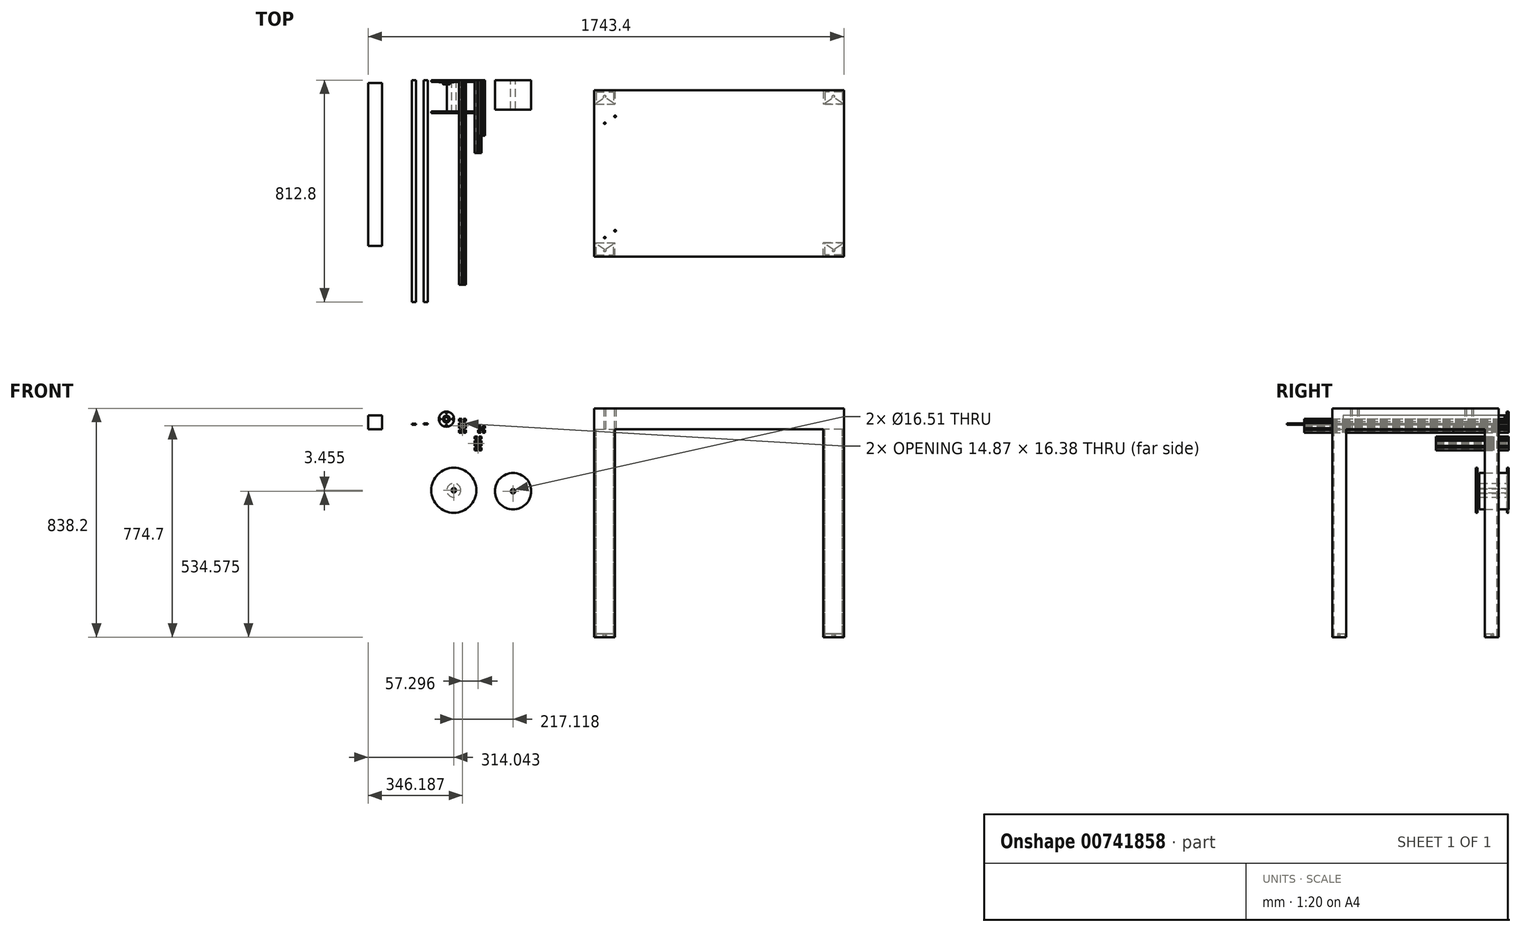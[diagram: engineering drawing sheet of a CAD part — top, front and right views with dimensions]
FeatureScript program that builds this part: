
annotation { "Feature Type Name" : "Feature", "Feature Type Description" : "" }
export const myFeature = defineFeature(function(context is Context, id is Id, definition is map)
    precondition{}
    {
        {
            var Q0;
            Q0=qCreatedBy(makeId("Front.planeOp"),FACE);
            var sketch = newSketch(context, id + "F0", { "sketchPlane" : qUnion([Q0])});
            skCircle(sketch, "E0", {"center": v(0, 0) * mm, "radius": 2.6 * mm});
            skLineSegment(sketch, "E1.bottom", {"start": v(-4.5, 4.5) * mm, "end": v(4.5, 4.5) * mm});
            skLineSegment(sketch, "E1.top", {"start": v(-4.5, -4.5) * mm, "end": v(4.5, -4.5) * mm});
            skLineSegment(sketch, "E1.left", {"start": v(-4.5, 4.5) * mm, "end": v(-4.5, -4.5) * mm});
            skLineSegment(sketch, "E1.right", {"start": v(4.5, 4.5) * mm, "end": v(4.5, -4.5) * mm});
            skLineSegment(sketch, "E2.bottom", {"start": v(-12.7, 12.7) * mm, "end": v(12.7, 12.7) * mm});
            skLineSegment(sketch, "E2.top", {"start": v(-12.7, -12.7) * mm, "end": v(12.7, -12.7) * mm});
            skLineSegment(sketch, "E2.left", {"start": v(-12.7, 12.7) * mm, "end": v(-12.7, -12.7) * mm});
            skLineSegment(sketch, "E2.right", {"start": v(12.7, 12.7) * mm, "end": v(12.7, -12.7) * mm});
            skLineSegment(sketch, "E3.bottom", {"start": v(-3.24, 12.7) * mm, "end": v(3.24, 12.7) * mm});
            skLineSegment(sketch, "E3.top", {"start": v(-3.24, 4.5) * mm, "end": v(3.24, 4.5) * mm});
            skLineSegment(sketch, "E3.left", {"start": v(-3.24, 12.7) * mm, "end": v(-3.24, 10.5) * mm});
            skLineSegment(sketch, "E3.right", {"start": v(3.24, 12.7) * mm, "end": v(3.24, 10.5) * mm});
            skLineSegment(sketch, "E4.bottom", {"start": v(-7.43, 10.5) * mm, "end": v(-3.24, 10.5) * mm});
            skLineSegment(sketch, "E5", {"start": v(-7.43, 10.5) * mm, "end": v(-3.24, 4.5) * mm});
            skLineSegment(sketch, "E6", {"start": v(3.24, 4.5) * mm, "end": v(7.43, 10.5) * mm});
            skLineSegment(sketch, "E7.trimOffspring", {"start": v(3.24, 10.5) * mm, "end": v(7.43, 10.5) * mm});
            skLineSegment(sketch, "E8.bottom", {"start": v(-12.7, 3.24) * mm, "end": v(-10.5, 3.24) * mm});
            skLineSegment(sketch, "E8.top", {"start": v(-12.7, -3.24) * mm, "end": v(-10.5, -3.24) * mm});
            skLineSegment(sketch, "E8.left", {"start": v(-12.7, 3.24) * mm, "end": v(-12.7, -3.24) * mm});
            skLineSegment(sketch, "E8.right", {"start": v(-4.5, 3.24) * mm, "end": v(-4.5, -3.24) * mm});
            skLineSegment(sketch, "E9.left", {"start": v(-10.5, 7.43) * mm, "end": v(-10.5, 3.24) * mm});
            skLineSegment(sketch, "E10", {"start": v(-10.5, 7.43) * mm, "end": v(-4.5, 3.24) * mm});
            skLineSegment(sketch, "E11.trimOffspring", {"start": v(-10.5, -3.24) * mm, "end": v(-10.5, -7.43) * mm});
            skLineSegment(sketch, "E12.MirrorCS", {"start": v(-3.24, -12.7) * mm, "end": v(-3.24, -10.5) * mm});
            skLineSegment(sketch, "E13.MirrorCS", {"start": v(-7.43, -10.5) * mm, "end": v(-3.24, -10.5) * mm});
            skLineSegment(sketch, "E14.MirrorCS", {"start": v(-7.43, -10.5) * mm, "end": v(-3.24, -4.5) * mm});
            skLineSegment(sketch, "E15.MirrorCS", {"start": v(3.24, -4.5) * mm, "end": v(7.43, -10.5) * mm});
            skLineSegment(sketch, "E16.MirrorCS", {"start": v(3.24, -10.5) * mm, "end": v(7.43, -10.5) * mm});
            skLineSegment(sketch, "E17.MirrorCS", {"start": v(3.24, -12.7) * mm, "end": v(3.24, -10.5) * mm});
            skLineSegment(sketch, "E18.MirrorCS", {"start": v(10.5, 7.43) * mm, "end": v(4.5, 3.24) * mm});
            skLineSegment(sketch, "E19.MirrorCS", {"start": v(10.5, -3.24) * mm, "end": v(10.5, -7.43) * mm});
            skLineSegment(sketch, "E20.MirrorCS", {"start": v(12.7, -3.24) * mm, "end": v(10.5, -3.24) * mm});
            skLineSegment(sketch, "E21.MirrorCS", {"start": v(12.7, 3.24) * mm, "end": v(10.5, 3.24) * mm});
            skLineSegment(sketch, "E22.MirrorCS", {"start": v(10.5, 7.43) * mm, "end": v(10.5, 3.24) * mm});
            skLineSegment(sketch, "E23", {"start": v(-10.5, -7.43) * mm, "end": v(-4.5, -3.24) * mm});
            skLineSegment(sketch, "E24", {"start": v(4.5, -3.24) * mm, "end": v(10.5, -7.43) * mm});
            skCircle(sketch, "E25", {"center": v(0, 25.4) * mm, "radius": 2.6 * mm});
            skLineSegment(sketch, "E26.bottom", {"start": v(-4.5, 29.9) * mm, "end": v(4.5, 29.9) * mm});
            skLineSegment(sketch, "E26.top", {"start": v(-4.5, 20.9) * mm, "end": v(4.5, 20.9) * mm});
            skLineSegment(sketch, "E26.left", {"start": v(-4.5, 29.9) * mm, "end": v(-4.5, 20.9) * mm});
            skLineSegment(sketch, "E26.right", {"start": v(4.5, 29.9) * mm, "end": v(4.5, 20.9) * mm});
            skLineSegment(sketch, "E27.bottom", {"start": v(-12.7, 38.1) * mm, "end": v(12.7, 38.1) * mm});
            skLineSegment(sketch, "E27.left", {"start": v(-12.7, 38.1) * mm, "end": v(-12.7, 12.7) * mm});
            skLineSegment(sketch, "E27.right", {"start": v(12.7, 38.1) * mm, "end": v(12.7, 12.7) * mm});
            skLineSegment(sketch, "E28.bottom", {"start": v(-3.24, 38.1) * mm, "end": v(3.24, 38.1) * mm});
            skLineSegment(sketch, "E28.top", {"start": v(-3.24, 29.9) * mm, "end": v(3.24, 29.9) * mm});
            skLineSegment(sketch, "E28.left", {"start": v(-3.24, 38.1) * mm, "end": v(-3.24, 35.9) * mm});
            skLineSegment(sketch, "E28.right", {"start": v(3.24, 38.1) * mm, "end": v(3.24, 35.9) * mm});
            skLineSegment(sketch, "E29.bottom", {"start": v(-7.44, 35.9) * mm, "end": v(-3.24, 35.9) * mm});
            skLineSegment(sketch, "E30", {"start": v(-7.44, 35.9) * mm, "end": v(-3.24, 29.9) * mm});
            skLineSegment(sketch, "E31", {"start": v(3.24, 29.9) * mm, "end": v(7.42, 35.9) * mm});
            skLineSegment(sketch, "E32.trimOffspring", {"start": v(3.24, 35.9) * mm, "end": v(7.42, 35.9) * mm});
            skLineSegment(sketch, "E33.bottom", {"start": v(-12.7, 28.64) * mm, "end": v(-10.5, 28.64) * mm});
            skLineSegment(sketch, "E33.top", {"start": v(-12.7, 22.16) * mm, "end": v(-10.5, 22.16) * mm});
            skLineSegment(sketch, "E33.left", {"start": v(-12.7, 28.64) * mm, "end": v(-12.7, 22.16) * mm});
            skLineSegment(sketch, "E33.right", {"start": v(-4.5, 28.64) * mm, "end": v(-4.5, 22.16) * mm});
            skLineSegment(sketch, "E34.left", {"start": v(-10.5, 32.86) * mm, "end": v(-10.5, 28.64) * mm});
            skLineSegment(sketch, "E35", {"start": v(-10.5, 32.86) * mm, "end": v(-4.5, 28.64) * mm});
            skLineSegment(sketch, "E36.trimOffspring", {"start": v(-10.5, 22.16) * mm, "end": v(-10.5, 18) * mm});
            skLineSegment(sketch, "E37.MirrorCS", {"start": v(-3.25, 12.73) * mm, "end": v(-3.25, 14.94) * mm});
            skLineSegment(sketch, "E38.MirrorCS", {"start": v(-7.44, 14.94) * mm, "end": v(-3.25, 14.94) * mm});
            skLineSegment(sketch, "E39.MirrorCS", {"start": v(-7.44, 14.94) * mm, "end": v(-3.25, 20.92) * mm});
            skLineSegment(sketch, "E40.MirrorCS", {"start": v(3.23, 20.92) * mm, "end": v(7.42, 14.94) * mm});
            skLineSegment(sketch, "E41.MirrorCS", {"start": v(3.23, 14.94) * mm, "end": v(7.42, 14.94) * mm});
            skLineSegment(sketch, "E42.MirrorCS", {"start": v(3.23, 12.73) * mm, "end": v(3.23, 14.94) * mm});
            skLineSegment(sketch, "E43", {"start": v(-10.5, 18) * mm, "end": v(-4.5, 22.16) * mm});
            skLineSegment(sketch, "E44", {"start": v(-7.44, 14.94) * mm, "end": v(-7.43, 10.5) * mm});
            skLineSegment(sketch, "E45", {"start": v(7.42, 14.94) * mm, "end": v(7.43, 10.5) * mm});
            skLineSegment(sketch, "E46", {"start": v(0, 25.4) * mm, "end": v(0, 29.9) * mm});
            skLineSegment(sketch, "E47.MirrorCS", {"start": v(10.5, 32.86) * mm, "end": v(4.5, 28.64) * mm});
            skLineSegment(sketch, "E48.MirrorCS", {"start": v(10.5, 32.86) * mm, "end": v(10.5, 28.64) * mm});
            skLineSegment(sketch, "E49.MirrorCS", {"start": v(12.7, 28.64) * mm, "end": v(10.5, 28.64) * mm});
            skLineSegment(sketch, "E50.MirrorCS", {"start": v(12.7, 22.16) * mm, "end": v(10.5, 22.16) * mm});
            skLineSegment(sketch, "E51.MirrorCS", {"start": v(10.5, 22.16) * mm, "end": v(10.5, 18) * mm});
            skLineSegment(sketch, "E52.MirrorCS", {"start": v(10.5, 18) * mm, "end": v(4.5, 22.16) * mm});
            skSolve(sketch);
        }
        {
            var Q0;
            Q0=makeQuery(id+"F0.imprint","IMPRINT",FACE,{"disambiguationData":[TD([[makeQuery(id+"F0.imprint","IMPRINT",EDGE,{"derivedFrom":sQuery(id+"F0.wireOp",EDGE,"E0")}),-1.0]])]});
            var Q1;
            {var subQ0=sQuery(id+"F0.wireOp",EDGE,"E8.top");Q1=makeQuery(id+"F0.imprint","IMPRINT",FACE,{"disambiguationData":[TD([[makeQuery(id+"F0.imprint","IMPRINT",EDGE,{"derivedFrom":subQ0}),-1.0]])]});}
            var Q2;
            {var subQ9=sQuery(id+"F0.wireOp",EDGE,"E15.MirrorCS");Q2=makeQuery(id+"F0.imprint","IMPRINT",FACE,{"disambiguationData":[TD([[makeQuery(id+"F0.imprint","IMPRINT",EDGE,{"derivedFrom":subQ9}),1.0]])]});}
            var Q3;
            {var subQ1=sQuery(id+"F0.wireOp",EDGE,"E5");Q3=makeQuery(id+"F0.imprint","IMPRINT",FACE,{"disambiguationData":[TD([[makeQuery(id+"F0.imprint","IMPRINT",EDGE,{"derivedFrom":subQ1}),-1.0]])]});}
            var Q4;
            {var subQ0=sQuery(id+"F0.wireOp",EDGE,"E33.top");Q4=makeQuery(id+"F0.imprint","IMPRINT",FACE,{"disambiguationData":[TD([[makeQuery(id+"F0.imprint","IMPRINT",EDGE,{"derivedFrom":subQ0}),-1.0]])]});}
            var Q5;
            {var subQ3=sQuery(id+"F0.wireOp",EDGE,"E6");Q5=makeQuery(id+"F0.imprint","IMPRINT",FACE,{"disambiguationData":[TD([[makeQuery(id+"F0.imprint","IMPRINT",EDGE,{"derivedFrom":subQ3}),-1.0]])]});}
            var Q6;
            {var subQ1=sQuery(id+"F0.wireOp",EDGE,"E28.left");Q6=makeQuery(id+"F0.imprint","IMPRINT",FACE,{"disambiguationData":[TD([[makeQuery(id+"F0.imprint","IMPRINT",EDGE,{"derivedFrom":subQ1}),-1.0]])]});}
            var Q7;
            Q7=makeQuery(id+"F0.imprint","IMPRINT",FACE,{"disambiguationData":[TD([[makeQuery(id+"F0.imprint","IMPRINT",EDGE,{"derivedFrom":sQuery(id+"F0.wireOp",EDGE,"E25")}),-1.0]])]});
            var Q8;
            {var subQ5=sQuery(id+"F0.wireOp",EDGE,"E28.right");Q8=makeQuery(id+"F0.imprint","IMPRINT",FACE,{"disambiguationData":[TD([[makeQuery(id+"F0.imprint","IMPRINT",EDGE,{"derivedFrom":subQ5}),1.0]])]});}
            var Q9;
            {var subQ10=sQuery(id+"F0.wireOp",EDGE,"E50.MirrorCS");Q9=makeQuery(id+"F0.imprint","IMPRINT",FACE,{"disambiguationData":[TD([[makeQuery(id+"F0.imprint","IMPRINT",EDGE,{"derivedFrom":subQ10}),1.0]])]});}
            extrude(context, id + "F1", {"entities" : qUnion([Q0, Q1, Q2, Q3, Q4, Q5, Q6, Q7, Q8, Q9]), "depth" : 749.3 * mm, "offsetDistance" : 25.4 * mm});
        }
        {
            var Q0;
            Q0=qCreatedBy(makeId("Front.planeOp"),FACE);
            var sketch = newSketch(context, id + "F2", { "sketchPlane" : qUnion([Q0])});
            skCircle(sketch, "E53", {"center": v(69.72, 0.13) * mm, "radius": 2.6 * mm});
            skLineSegment(sketch, "E54.bottom", {"start": v(65.21, 4.64) * mm, "end": v(74.23, 4.64) * mm});
            skLineSegment(sketch, "E54.top", {"start": v(65.21, -4.38) * mm, "end": v(74.23, -4.38) * mm});
            skLineSegment(sketch, "E54.left", {"start": v(65.21, 4.64) * mm, "end": v(65.21, -4.38) * mm});
            skLineSegment(sketch, "E54.right", {"start": v(74.23, 4.64) * mm, "end": v(74.23, -4.38) * mm});
            skLineSegment(sketch, "E55.bottom", {"start": v(57.02, 12.83) * mm, "end": v(82.42, 12.83) * mm});
            skLineSegment(sketch, "E55.top", {"start": v(57.02, -12.57) * mm, "end": v(82.42, -12.57) * mm});
            skLineSegment(sketch, "E55.left", {"start": v(57.02, 12.83) * mm, "end": v(57.02, -12.57) * mm});
            skLineSegment(sketch, "E55.right", {"start": v(82.42, 12.83) * mm, "end": v(82.42, -12.57) * mm});
            skLineSegment(sketch, "E56.bottom", {"start": v(66.48, 12.83) * mm, "end": v(72.96, 12.83) * mm});
            skLineSegment(sketch, "E56.top", {"start": v(66.48, 4.64) * mm, "end": v(72.96, 4.64) * mm});
            skLineSegment(sketch, "E56.left", {"start": v(66.48, 12.83) * mm, "end": v(66.48, 10.62) * mm});
            skLineSegment(sketch, "E56.right", {"start": v(72.96, 12.83) * mm, "end": v(72.96, 10.62) * mm});
            skLineSegment(sketch, "E57.bottom", {"start": v(62.3, 10.62) * mm, "end": v(66.48, 10.62) * mm});
            skLineSegment(sketch, "E58", {"start": v(62.3, 10.62) * mm, "end": v(66.48, 4.64) * mm});
            skLineSegment(sketch, "E59", {"start": v(72.96, 4.64) * mm, "end": v(77.15, 10.62) * mm});
            skLineSegment(sketch, "E60.trimOffspring", {"start": v(72.96, 10.62) * mm, "end": v(77.15, 10.62) * mm});
            skLineSegment(sketch, "E61.bottom", {"start": v(57.02, 3.37) * mm, "end": v(59.23, 3.37) * mm});
            skLineSegment(sketch, "E61.top", {"start": v(57.02, -3.1) * mm, "end": v(59.23, -3.1) * mm});
            skLineSegment(sketch, "E61.left", {"start": v(57.02, 3.37) * mm, "end": v(57.02, -3.1) * mm});
            skLineSegment(sketch, "E61.right", {"start": v(65.21, 3.37) * mm, "end": v(65.21, -3.1) * mm});
            skLineSegment(sketch, "E62.left", {"start": v(59.23, 7.56) * mm, "end": v(59.23, 3.37) * mm});
            skLineSegment(sketch, "E63", {"start": v(59.23, 7.56) * mm, "end": v(65.21, 3.37) * mm});
            skLineSegment(sketch, "E64.trimOffspring", {"start": v(59.23, -3.1) * mm, "end": v(59.23, -7.3) * mm});
            skLineSegment(sketch, "E65.MirrorCS", {"start": v(66.48, -12.57) * mm, "end": v(66.48, -10.36) * mm});
            skLineSegment(sketch, "E66.MirrorCS", {"start": v(62.3, -10.36) * mm, "end": v(66.48, -10.36) * mm});
            skLineSegment(sketch, "E67.MirrorCS", {"start": v(62.3, -10.36) * mm, "end": v(66.48, -4.38) * mm});
            skLineSegment(sketch, "E68.MirrorCS", {"start": v(72.96, -4.38) * mm, "end": v(77.15, -10.36) * mm});
            skLineSegment(sketch, "E69.MirrorCS", {"start": v(72.96, -10.36) * mm, "end": v(77.15, -10.36) * mm});
            skLineSegment(sketch, "E70.MirrorCS", {"start": v(72.96, -12.57) * mm, "end": v(72.96, -10.36) * mm});
            skLineSegment(sketch, "E71.MirrorCS", {"start": v(80.21, 7.56) * mm, "end": v(74.23, 3.37) * mm});
            skLineSegment(sketch, "E72.MirrorCS", {"start": v(80.21, 4.3) * mm, "end": v(80.21, -7.3) * mm});
            skLineSegment(sketch, "E73.MirrorCS", {"start": v(82.42, -3.1) * mm, "end": v(80.21, -3.1) * mm});
            skLineSegment(sketch, "E74.MirrorCS", {"start": v(82.42, 3.37) * mm, "end": v(80.21, 3.37) * mm});
            skLineSegment(sketch, "E75.MirrorCS", {"start": v(80.21, 7.56) * mm, "end": v(80.21, 3.37) * mm});
            skLineSegment(sketch, "E76", {"start": v(59.23, -7.3) * mm, "end": v(65.21, -3.1) * mm});
            skLineSegment(sketch, "E77", {"start": v(74.23, -3.1) * mm, "end": v(80.21, -7.3) * mm});
            skSolve(sketch);
        }
        {
            var Q0;
            {var subQ0=sQuery(id+"F2.wireOp",EDGE,"E61.top");Q0=makeQuery(id+"F2.imprint","IMPRINT",FACE,{"disambiguationData":[TD([[makeQuery(id+"F2.imprint","IMPRINT",EDGE,{"derivedFrom":subQ0}),-1.0]])]});}
            var Q1;
            {var subQ1=sQuery(id+"F2.wireOp",EDGE,"E56.left");Q1=makeQuery(id+"F2.imprint","IMPRINT",FACE,{"disambiguationData":[TD([[makeQuery(id+"F2.imprint","IMPRINT",EDGE,{"derivedFrom":subQ1}),-1.0]])]});}
            var Q2;
            {var subQ3=sQuery(id+"F2.wireOp",EDGE,"E56.right");Q2=makeQuery(id+"F2.imprint","IMPRINT",FACE,{"disambiguationData":[TD([[makeQuery(id+"F2.imprint","IMPRINT",EDGE,{"derivedFrom":subQ3}),1.0]])]});}
            var Q3;
            {var subQ9=sQuery(id+"F2.wireOp",EDGE,"E68.MirrorCS");Q3=makeQuery(id+"F2.imprint","IMPRINT",FACE,{"disambiguationData":[TD([[makeQuery(id+"F2.imprint","IMPRINT",EDGE,{"derivedFrom":subQ9}),1.0]])]});}
            var Q4;
            Q4=makeQuery(id+"F2.imprint","IMPRINT",FACE,{"disambiguationData":[TD([[makeQuery(id+"F2.imprint","IMPRINT",EDGE,{"derivedFrom":sQuery(id+"F2.wireOp",EDGE,"E53")}),-1.0]])]});
            extrude(context, id + "F3", {"entities" : qUnion([Q0, Q1, Q2, Q3, Q4]), "depth" : 203.2 * mm, "offsetDistance" : 25.4 * mm});
        }
        {
            var Q0;
            Q0=qCreatedBy(makeId("Front.planeOp"),FACE);
            var sketch = newSketch(context, id + "F4", { "sketchPlane" : qUnion([Q0])});
            skCircle(sketch, "E78", {"center": v(-59.23, 36.74) * mm, "radius": 27.78 * mm});
            skCircle(sketch, "E79", {"center": v(-59.23, 36.74) * mm, "radius": 23.81 * mm});
            skCircle(sketch, "E80", {"center": v(-59.23, 60.55) * mm, "radius": 3.18 * mm});
            skCircle(sketch, "E81", {"center": v(-83.04, 36.74) * mm, "radius": 3.18 * mm});
            skCircle(sketch, "E82", {"center": v(-59.23, 12.93) * mm, "radius": 3.18 * mm});
            skCircle(sketch, "E83", {"center": v(-35.42, 36.74) * mm, "radius": 3.18 * mm});
            skCircle(sketch, "E84", {"center": v(-59.23, 36.74) * mm, "radius": 6.86 * mm});
            skLineSegment(sketch, "E85", {"start": v(-59.23, 36.74) * mm, "end": v(-83.04, 36.74) * mm});
            skLineSegment(sketch, "E86", {"start": v(-59.23, 36.74) * mm, "end": v(-59.23, 60.55) * mm});
            skSolve(sketch);
        }
        {
            var Q0;
            Q0=makeQuery(id+"F4.imprint","IMPRINT",FACE,{"disambiguationData":[TD([[makeQuery(id+"F4.imprint","IMPRINT",EDGE,{"derivedFrom":sQuery(id+"F4.wireOp",EDGE,"E78")}),1.0]])]});
            var Q1;
            {var subQ5=sQuery(id+"F4.wireOp",EDGE,"E80");var subQ6=sQuery(id+"F4.wireOp",EDGE,"E79");var subQ7=makeQuery(id+"F4.imprint","INTERSECT",VERTEX,{"disambiguationData":[OD(1.0)],"derivedFrom":[subQ6,subQ5]});Q1=makeQuery(id+"F4.imprint","IMPRINT",FACE,{"disambiguationData":[TD([[makeQuery(id+"F4.imprint","IMPRINT",EDGE,{"disambiguationData":[TD([[subQ7,-1.0]])],"derivedFrom":subQ6}),1.0]])]});}
            var Q2;
            {var subQ1=sQuery(id+"F4.wireOp",EDGE,"E79");var subQ5=sQuery(id+"F4.wireOp",EDGE,"E80");var subQ6=makeQuery(id+"F4.imprint","INTERSECT",VERTEX,{"disambiguationData":[OD(0.0)],"derivedFrom":[subQ1,subQ5]});Q2=makeQuery(id+"F4.imprint","IMPRINT",FACE,{"disambiguationData":[TD([[makeQuery(id+"F4.imprint","IMPRINT",EDGE,{"disambiguationData":[TD([[subQ6,1.0]])],"derivedFrom":subQ1}),1.0]])]});}
            extrude(context, id + "F5", {"entities" : qUnion([Q0, Q1, Q2]), "depth" : 7.94 * mm, "offsetDistance" : 25.4 * mm});
        }
        {
            var Q0;
            Q0=makeQuery(id+"F5.opExtrude","CAP_FACE",FACE,{"disambiguationData":[OSD([sQuery(id+"F4.wireOp",EDGE,"E78"),sQuery(id+"F4.wireOp",EDGE,"E80"),sQuery(id+"F4.wireOp",EDGE,"E81"),sQuery(id+"F4.wireOp",EDGE,"E82"),sQuery(id+"F4.wireOp",EDGE,"E83"),sQuery(id+"F4.wireOp",EDGE,"E84")])],"isStart":false});
            var sketch = newSketch(context, id + "F6", { "sketchPlane" : qUnion([Q0])});
            skCircle(sketch, "E87", {"center": v(-59.23, 36.74) * mm, "radius": 6.86 * mm});
            skCircle(sketch, "E88", {"center": v(-59.23, 36.74) * mm, "radius": 12.7 * mm});
            skSolve(sketch);
        }
        {
            var Q0;
            Q0=makeQuery(id+"F6.imprint","IMPRINT",FACE,{"disambiguationData":[TD([[makeQuery(id+"F6.imprint","IMPRINT",EDGE,{"derivedFrom":sQuery(id+"F6.wireOp",EDGE,"E87")}),-1.0]])]});
            extrude(context, id + "F7", {"entities" : qUnion([Q0]), "operationType" : NewBodyOperationType.ADD, "depth" : 7.94 * mm, "offsetDistance" : 25.4 * mm});
        }
        {
            var Q0;
            Q0=makeQuery(id+"F7.opExtrude","CAP_EDGE",EDGE,{"disambiguationData":[OSD([sQuery(id+"F6.wireOp",EDGE,"E88")])],"isStart":false});
            var Q1;
            Q1=makeQuery(id+"F7.opExtrude","CAP_EDGE",EDGE,{"disambiguationData":[OSD([sQuery(id+"F6.wireOp",EDGE,"E88")])],"isStart":true});
            fillet(context, id + "F8", {"entities" : qUnion([Q0, Q1]), "radius" : 1.27 * mm, "tangentPropagation" : true, "allowEdgeOverflow" : false});
        }
        {
            var Q0;
            Q0=qCreatedBy(makeId("Top.planeOp"),FACE);
            var sketch = newSketch(context, id + "F9", { "sketchPlane" : qUnion([Q0])});
            skLineSegment(sketch, "E89.bottom", {"start": v(482.81, -37.59) * mm, "end": v(1397.21, -37.59) * mm});
            skLineSegment(sketch, "E89.top", {"start": v(482.81, -647.19) * mm, "end": v(1397.21, -647.19) * mm});
            skLineSegment(sketch, "E89.left", {"start": v(482.81, -37.59) * mm, "end": v(482.81, -647.19) * mm});
            skLineSegment(sketch, "E89.right", {"start": v(1397.21, -37.59) * mm, "end": v(1397.21, -647.19) * mm});
            skLineSegment(sketch, "E90", {"start": v(559.01, 43.4) * mm, "end": v(559.01, -586.06) * mm});
            skLineSegment(sketch, "E91", {"start": v(520.91, 45.88) * mm, "end": v(520.91, -592.27) * mm});
            skCircle(sketch, "E92", {"center": v(559.01, -132.84) * mm, "radius": 3.18 * mm});
            skCircle(sketch, "E93", {"center": v(559.01, -551.94) * mm, "radius": 3.18 * mm});
            skCircle(sketch, "E94", {"center": v(520.91, -577.34) * mm, "radius": 2.78 * mm});
            skCircle(sketch, "E95", {"center": v(520.91, -158.24) * mm, "radius": 2.78 * mm});
            skSolve(sketch);
        }
        {
            var Q0;
            Q0=makeQuery(id+"F9.imprint","IMPRINT",FACE,{"disambiguationData":[TD([[makeQuery(id+"F9.imprint","IMPRINT",EDGE,{"derivedFrom":sQuery(id+"F9.wireOp",EDGE,"E89.bottom")}),-1.0]])]});
            extrude(context, id + "F10", {"entities" : qUnion([Q0]), "depth" : 76.2 * mm, "offsetDistance" : 25.4 * mm});
        }
        {
            var Q0;
            Q0=makeQuery(id+"F10.opExtrude","CAP_FACE",FACE,{"disambiguationData":[OSD([sQuery(id+"F9.wireOp",EDGE,"E89.bottom"),sQuery(id+"F9.wireOp",EDGE,"E89.top"),sQuery(id+"F9.wireOp",EDGE,"E89.left"),sQuery(id+"F9.wireOp",EDGE,"E89.right")])],"isStart":true});
            var sketch = newSketch(context, id + "F11", { "sketchPlane" : qUnion([Q0])});
            skLineSegment(sketch, "E96.bottom", {"start": v(482.81, 647.19) * mm, "end": v(559.01, 647.19) * mm});
            skLineSegment(sketch, "E96.top", {"start": v(482.81, 596.39) * mm, "end": v(559.01, 596.39) * mm});
            skLineSegment(sketch, "E96.left", {"start": v(482.81, 647.19) * mm, "end": v(482.81, 596.39) * mm});
            skLineSegment(sketch, "E96.right", {"start": v(559.01, 647.19) * mm, "end": v(559.01, 596.39) * mm});
            skLineSegment(sketch, "E97.bottom", {"start": v(482.81, 37.59) * mm, "end": v(559.01, 37.59) * mm});
            skLineSegment(sketch, "E97.top", {"start": v(482.81, 88.39) * mm, "end": v(559.01, 88.39) * mm});
            skLineSegment(sketch, "E97.left", {"start": v(482.81, 37.59) * mm, "end": v(482.81, 88.39) * mm});
            skLineSegment(sketch, "E97.right", {"start": v(559.01, 37.59) * mm, "end": v(559.01, 88.39) * mm});
            skLineSegment(sketch, "E98.bottom", {"start": v(1397.21, 37.59) * mm, "end": v(1321.01, 37.59) * mm});
            skLineSegment(sketch, "E98.top", {"start": v(1397.21, 88.39) * mm, "end": v(1321.01, 88.39) * mm});
            skLineSegment(sketch, "E98.left", {"start": v(1397.21, 37.59) * mm, "end": v(1397.21, 88.39) * mm});
            skLineSegment(sketch, "E98.right", {"start": v(1321.01, 37.59) * mm, "end": v(1321.01, 88.39) * mm});
            skLineSegment(sketch, "E99.bottom", {"start": v(1397.21, 647.19) * mm, "end": v(1321.01, 647.19) * mm});
            skLineSegment(sketch, "E99.top", {"start": v(1397.21, 596.39) * mm, "end": v(1321.01, 596.39) * mm});
            skLineSegment(sketch, "E99.left", {"start": v(1397.21, 647.19) * mm, "end": v(1397.21, 596.39) * mm});
            skLineSegment(sketch, "E99.right", {"start": v(1321.01, 647.19) * mm, "end": v(1321.01, 596.39) * mm});
            skLineSegment(sketch, "E100.0", {"start": v(1327.36, 43.94) * mm, "end": v(1327.36, 88.39) * mm});
            skLineSegment(sketch, "E100.1", {"start": v(1390.86, 43.94) * mm, "end": v(1327.36, 43.94) * mm});
            skLineSegment(sketch, "E100.2", {"start": v(1390.86, 43.94) * mm, "end": v(1390.86, 88.39) * mm});
            skLineSegment(sketch, "E101.0", {"start": v(489.16, 43.94) * mm, "end": v(489.16, 88.39) * mm});
            skLineSegment(sketch, "E101.1", {"start": v(489.16, 43.94) * mm, "end": v(552.66, 43.94) * mm});
            skLineSegment(sketch, "E101.2", {"start": v(552.66, 43.94) * mm, "end": v(552.66, 88.39) * mm});
            skLineSegment(sketch, "E102.0", {"start": v(489.16, 640.84) * mm, "end": v(489.16, 596.39) * mm});
            skLineSegment(sketch, "E102.1", {"start": v(489.16, 640.84) * mm, "end": v(552.66, 640.84) * mm});
            skLineSegment(sketch, "E102.2", {"start": v(552.66, 640.84) * mm, "end": v(552.66, 596.39) * mm});
            skLineSegment(sketch, "E103.0", {"start": v(1327.36, 640.84) * mm, "end": v(1327.36, 596.39) * mm});
            skLineSegment(sketch, "E103.1", {"start": v(1390.86, 640.84) * mm, "end": v(1327.36, 640.84) * mm});
            skLineSegment(sketch, "E103.2", {"start": v(1390.86, 640.84) * mm, "end": v(1390.86, 596.39) * mm});
            skSolve(sketch);
        }
        {
            var Q0;
            Q0=makeQuery(id+"F11.imprint","IMPRINT",FACE,{"disambiguationData":[TD([[makeQuery(id+"F11.imprint","IMPRINT",EDGE,{"derivedFrom":sQuery(id+"F11.wireOp",EDGE,"E96.bottom")}),-1.0]])]});
            var Q1;
            Q1=makeQuery(id+"F11.imprint","IMPRINT",FACE,{"disambiguationData":[TD([[makeQuery(id+"F11.imprint","IMPRINT",EDGE,{"derivedFrom":sQuery(id+"F11.wireOp",EDGE,"E97.bottom")}),1.0]])]});
            var Q2;
            Q2=makeQuery(id+"F11.imprint","IMPRINT",FACE,{"disambiguationData":[TD([[makeQuery(id+"F11.imprint","IMPRINT",EDGE,{"derivedFrom":sQuery(id+"F11.wireOp",EDGE,"E99.bottom")}),-1.0]])]});
            var Q3;
            Q3=makeQuery(id+"F11.imprint","IMPRINT",FACE,{"disambiguationData":[TD([[makeQuery(id+"F11.imprint","IMPRINT",EDGE,{"derivedFrom":sQuery(id+"F11.wireOp",EDGE,"E98.bottom")}),1.0]])]});
            extrude(context, id + "F12", {"entities" : qUnion([Q0, Q1, Q2, Q3]), "operationType" : NewBodyOperationType.ADD, "depth" : 762 * mm, "offsetDistance" : 25.4 * mm});
        }
        {
            var Q0;
            Q0=qCreatedBy(makeId("Front.planeOp"),FACE);
            var sketch = newSketch(context, id + "F13", { "sketchPlane" : qUnion([Q0])});
            skCircle(sketch, "E104", {"center": v(-32.15, -223.97) * mm, "radius": 82.55 * mm});
            skCircle(sketch, "E105", {"center": v(-32.15, -223.97) * mm, "radius": 8.26 * mm});
            skSolve(sketch);
        }
        {
            var Q0;
            Q0=makeQuery(id+"F13.imprint","IMPRINT",FACE,{"disambiguationData":[TD([[makeQuery(id+"F13.imprint","IMPRINT",EDGE,{"derivedFrom":sQuery(id+"F13.wireOp",EDGE,"E104")}),1.0]])]});
            extrude(context, id + "F14", {"entities" : qUnion([Q0]), "depth" : 6.35 * mm, "offsetDistance" : 25.4 * mm});
        }
        {
            var Q0;
            Q0=makeQuery(id+"F14.opExtrude","CAP_FACE",FACE,{"disambiguationData":[OSD([sQuery(id+"F13.wireOp",EDGE,"E104")])],"isStart":false});
            var sketch = newSketch(context, id + "F15", { "sketchPlane" : qUnion([Q0])});
            skCircle(sketch, "E106", {"center": v(-32.15, -223.97) * mm, "radius": 8.26 * mm});
            skCircle(sketch, "E107", {"center": v(-32.15, -223.97) * mm, "radius": 25.4 * mm});
            skSolve(sketch);
        }
        {
            var Q0;
            Q0=makeQuery(id+"F15.imprint","IMPRINT",FACE,{"disambiguationData":[TD([[makeQuery(id+"F15.imprint","IMPRINT",EDGE,{"derivedFrom":sQuery(id+"F15.wireOp",EDGE,"E106")}),-1.0]])]});
            extrude(context, id + "F16", {"entities" : qUnion([Q0]), "operationType" : NewBodyOperationType.ADD, "depth" : 107.95 * mm, "offsetDistance" : 25.4 * mm});
        }
        {
            var Q0;
            Q0=makeQuery(id+"F16.opExtrude","CAP_FACE",FACE,{"disambiguationData":[OSD([sQuery(id+"F15.wireOp",EDGE,"E106"),sQuery(id+"F15.wireOp",EDGE,"E107")])],"isStart":false});
            var sketch = newSketch(context, id + "F17", { "sketchPlane" : qUnion([Q0])});
            skCircle(sketch, "E108", {"center": v(-32.15, -223.97) * mm, "radius": 82.55 * mm});
            skCircle(sketch, "E109", {"center": v(-32.15, -223.97) * mm, "radius": 8.26 * mm});
            skSolve(sketch);
        }
        {
            var Q0;
            Q0=makeQuery(id+"F17.imprint","IMPRINT",FACE,{"disambiguationData":[TD([[makeQuery(id+"F17.imprint","IMPRINT",EDGE,{"derivedFrom":sQuery(id+"F17.wireOp",EDGE,"E108")}),1.0]])]});
            var Q1;
            Q1=makeQuery(id+"F17.imprint","IMPRINT",FACE,{"disambiguationData":[TD([[makeQuery(id+"F17.imprint","IMPRINT",EDGE,{"derivedFrom":sQuery(id+"F17.wireOp",EDGE,"E109")}),-1.0]])]});
            extrude(context, id + "F18", {"entities" : qUnion([Q0, Q1]), "operationType" : NewBodyOperationType.ADD, "depth" : 6.35 * mm, "offsetDistance" : 25.4 * mm});
        }
        {
            var Q0;
            Q0=qCreatedBy(makeId("Front.planeOp"),FACE);
            var sketch = newSketch(context, id + "F19", { "sketchPlane" : qUnion([Q0])});
            skCircle(sketch, "E110", {"center": v(184.97, -227.42) * mm, "radius": 66.67 * mm});
            skCircle(sketch, "E111", {"center": v(184.97, -227.42) * mm, "radius": 8.26 * mm});
            skSolve(sketch);
        }
        {
            var Q0;
            Q0=makeQuery(id+"F19.imprint","IMPRINT",FACE,{"disambiguationData":[TD([[makeQuery(id+"F19.imprint","IMPRINT",EDGE,{"derivedFrom":sQuery(id+"F19.wireOp",EDGE,"E110")}),1.0]])]});
            extrude(context, id + "F20", {"entities" : qUnion([Q0]), "depth" : 107.95 * mm, "offsetDistance" : 25.4 * mm});
        }
        {
            var Q0;
            Q0=qCreatedBy(makeId("Front.planeOp"),FACE);
            var sketch = newSketch(context, id + "F21", { "sketchPlane" : qUnion([Q0])});
            skCircle(sketch, "E112", {"center": v(57.3, -64.65) * mm, "radius": 2.6 * mm});
            skLineSegment(sketch, "E113.bottom", {"start": v(52.79, -60.14) * mm, "end": v(61.8, -60.14) * mm});
            skLineSegment(sketch, "E113.top", {"start": v(52.79, -69.15) * mm, "end": v(61.8, -69.15) * mm});
            skLineSegment(sketch, "E113.left", {"start": v(52.79, -60.14) * mm, "end": v(52.79, -69.15) * mm});
            skLineSegment(sketch, "E113.right", {"start": v(61.8, -60.14) * mm, "end": v(61.8, -69.15) * mm});
            skLineSegment(sketch, "E114.bottom", {"start": v(44.6, -51.95) * mm, "end": v(70, -51.95) * mm});
            skLineSegment(sketch, "E114.top", {"start": v(44.6, -77.35) * mm, "end": v(70, -77.35) * mm});
            skLineSegment(sketch, "E114.left", {"start": v(44.6, -51.95) * mm, "end": v(44.6, -77.35) * mm});
            skLineSegment(sketch, "E114.right", {"start": v(70, -51.95) * mm, "end": v(70, -77.35) * mm});
            skLineSegment(sketch, "E115.bottom", {"start": v(54.06, -51.95) * mm, "end": v(60.53, -51.95) * mm});
            skLineSegment(sketch, "E115.top", {"start": v(54.06, -60.14) * mm, "end": v(60.53, -60.14) * mm});
            skLineSegment(sketch, "E115.left", {"start": v(54.06, -51.95) * mm, "end": v(54.06, -54.15) * mm});
            skLineSegment(sketch, "E115.right", {"start": v(60.53, -51.95) * mm, "end": v(60.53, -54.15) * mm});
            skLineSegment(sketch, "E116.bottom", {"start": v(49.87, -54.15) * mm, "end": v(54.06, -54.15) * mm});
            skLineSegment(sketch, "E117", {"start": v(49.87, -54.15) * mm, "end": v(54.06, -60.14) * mm});
            skLineSegment(sketch, "E118", {"start": v(60.53, -60.14) * mm, "end": v(64.73, -54.15) * mm});
            skLineSegment(sketch, "E119.trimOffspring", {"start": v(60.53, -54.15) * mm, "end": v(64.73, -54.15) * mm});
            skLineSegment(sketch, "E120.bottom", {"start": v(44.6, -61.4) * mm, "end": v(46.8, -61.4) * mm});
            skLineSegment(sketch, "E120.top", {"start": v(44.6, -67.88) * mm, "end": v(46.8, -67.88) * mm});
            skLineSegment(sketch, "E120.left", {"start": v(44.6, -61.4) * mm, "end": v(44.6, -67.88) * mm});
            skLineSegment(sketch, "E120.right", {"start": v(52.79, -61.4) * mm, "end": v(52.79, -67.88) * mm});
            skLineSegment(sketch, "E121.left", {"start": v(46.8, -57.22) * mm, "end": v(46.8, -61.4) * mm});
            skLineSegment(sketch, "E122", {"start": v(46.8, -57.22) * mm, "end": v(52.79, -61.4) * mm});
            skLineSegment(sketch, "E123.trimOffspring", {"start": v(46.8, -67.88) * mm, "end": v(46.8, -72.07) * mm});
            skLineSegment(sketch, "E124.MirrorCS", {"start": v(54.06, -77.35) * mm, "end": v(54.06, -75.14) * mm});
            skLineSegment(sketch, "E125.MirrorCS", {"start": v(49.87, -75.14) * mm, "end": v(54.06, -75.14) * mm});
            skLineSegment(sketch, "E126.MirrorCS", {"start": v(49.87, -75.14) * mm, "end": v(54.06, -69.15) * mm});
            skLineSegment(sketch, "E127.MirrorCS", {"start": v(60.53, -69.15) * mm, "end": v(64.73, -75.14) * mm});
            skLineSegment(sketch, "E128.MirrorCS", {"start": v(60.53, -75.14) * mm, "end": v(64.73, -75.14) * mm});
            skLineSegment(sketch, "E129.MirrorCS", {"start": v(60.53, -77.35) * mm, "end": v(60.53, -75.14) * mm});
            skLineSegment(sketch, "E130.MirrorCS", {"start": v(67.79, -57.22) * mm, "end": v(61.8, -61.4) * mm});
            skLineSegment(sketch, "E131.MirrorCS", {"start": v(67.79, -67.88) * mm, "end": v(67.79, -72.07) * mm});
            skLineSegment(sketch, "E132.MirrorCS", {"start": v(70, -67.88) * mm, "end": v(67.79, -67.88) * mm});
            skLineSegment(sketch, "E133.MirrorCS", {"start": v(70, -61.4) * mm, "end": v(67.79, -61.4) * mm});
            skLineSegment(sketch, "E134.MirrorCS", {"start": v(67.79, -57.22) * mm, "end": v(67.79, -61.4) * mm});
            skLineSegment(sketch, "E135", {"start": v(46.8, -72.07) * mm, "end": v(52.79, -67.88) * mm});
            skLineSegment(sketch, "E136", {"start": v(61.8, -67.88) * mm, "end": v(67.79, -72.07) * mm});
            skCircle(sketch, "E137", {"center": v(57.3, -39.25) * mm, "radius": 2.6 * mm});
            skLineSegment(sketch, "E138.bottom", {"start": v(52.79, -34.74) * mm, "end": v(61.8, -34.74) * mm});
            skLineSegment(sketch, "E138.top", {"start": v(52.79, -43.75) * mm, "end": v(61.8, -43.75) * mm});
            skLineSegment(sketch, "E138.left", {"start": v(52.79, -34.74) * mm, "end": v(52.79, -43.75) * mm});
            skLineSegment(sketch, "E138.right", {"start": v(61.8, -34.74) * mm, "end": v(61.8, -43.75) * mm});
            skLineSegment(sketch, "E139.bottom", {"start": v(44.6, -26.55) * mm, "end": v(70, -26.55) * mm});
            skLineSegment(sketch, "E139.left", {"start": v(44.6, -26.55) * mm, "end": v(44.6, -51.95) * mm});
            skLineSegment(sketch, "E139.right", {"start": v(70, -26.55) * mm, "end": v(70, -51.95) * mm});
            skLineSegment(sketch, "E140.bottom", {"start": v(54.06, -26.55) * mm, "end": v(60.53, -26.55) * mm});
            skLineSegment(sketch, "E140.top", {"start": v(54.06, -34.74) * mm, "end": v(60.53, -34.74) * mm});
            skLineSegment(sketch, "E140.left", {"start": v(54.06, -26.55) * mm, "end": v(54.06, -28.75) * mm});
            skLineSegment(sketch, "E140.right", {"start": v(60.53, -26.55) * mm, "end": v(60.53, -28.75) * mm});
            skLineSegment(sketch, "E141.bottom", {"start": v(49.86, -28.75) * mm, "end": v(54.06, -28.75) * mm});
            skLineSegment(sketch, "E142", {"start": v(49.86, -28.75) * mm, "end": v(54.06, -34.74) * mm});
            skLineSegment(sketch, "E143", {"start": v(60.53, -34.74) * mm, "end": v(64.72, -28.75) * mm});
            skLineSegment(sketch, "E144.trimOffspring", {"start": v(60.53, -28.75) * mm, "end": v(64.72, -28.75) * mm});
            skLineSegment(sketch, "E145.bottom", {"start": v(44.6, -36) * mm, "end": v(46.8, -36) * mm});
            skLineSegment(sketch, "E145.top", {"start": v(44.6, -42.48) * mm, "end": v(46.8, -42.48) * mm});
            skLineSegment(sketch, "E145.left", {"start": v(44.6, -36) * mm, "end": v(44.6, -42.48) * mm});
            skLineSegment(sketch, "E145.right", {"start": v(52.79, -36) * mm, "end": v(52.79, -42.48) * mm});
            skLineSegment(sketch, "E146.left", {"start": v(46.8, -31.79) * mm, "end": v(46.8, -36) * mm});
            skLineSegment(sketch, "E147", {"start": v(46.8, -31.79) * mm, "end": v(52.79, -36) * mm});
            skLineSegment(sketch, "E148.trimOffspring", {"start": v(46.8, -42.48) * mm, "end": v(46.8, -46.65) * mm});
            skLineSegment(sketch, "E149.MirrorCS", {"start": v(54.05, -51.92) * mm, "end": v(54.05, -49.7) * mm});
            skLineSegment(sketch, "E150.MirrorCS", {"start": v(49.86, -49.7) * mm, "end": v(54.05, -49.7) * mm});
            skLineSegment(sketch, "E151.MirrorCS", {"start": v(49.86, -49.7) * mm, "end": v(54.05, -43.72) * mm});
            skLineSegment(sketch, "E152.MirrorCS", {"start": v(60.53, -43.72) * mm, "end": v(64.72, -49.7) * mm});
            skLineSegment(sketch, "E153.MirrorCS", {"start": v(60.53, -49.7) * mm, "end": v(64.72, -49.7) * mm});
            skLineSegment(sketch, "E154.MirrorCS", {"start": v(60.53, -51.92) * mm, "end": v(60.53, -49.7) * mm});
            skLineSegment(sketch, "E155", {"start": v(46.8, -46.65) * mm, "end": v(52.79, -42.48) * mm});
            skLineSegment(sketch, "E156", {"start": v(49.86, -49.7) * mm, "end": v(49.87, -54.15) * mm});
            skLineSegment(sketch, "E157", {"start": v(64.72, -49.7) * mm, "end": v(64.73, -54.15) * mm});
            skLineSegment(sketch, "E158", {"start": v(57.3, -39.25) * mm, "end": v(57.3, -34.74) * mm});
            skLineSegment(sketch, "E159.MirrorCS", {"start": v(67.79, -31.79) * mm, "end": v(61.8, -36) * mm});
            skLineSegment(sketch, "E160.MirrorCS", {"start": v(67.79, -31.79) * mm, "end": v(67.79, -36) * mm});
            skLineSegment(sketch, "E161.MirrorCS", {"start": v(70, -36) * mm, "end": v(67.79, -36) * mm});
            skLineSegment(sketch, "E162.MirrorCS", {"start": v(70, -42.48) * mm, "end": v(67.79, -42.48) * mm});
            skLineSegment(sketch, "E163.MirrorCS", {"start": v(67.79, -42.48) * mm, "end": v(67.79, -46.65) * mm});
            skLineSegment(sketch, "E164.MirrorCS", {"start": v(67.79, -46.65) * mm, "end": v(61.8, -42.48) * mm});
            skSolve(sketch);
        }
        {
            var Q0;
            {var subQ7=sQuery(id+"F21.wireOp",EDGE,"E127.MirrorCS");Q0=makeQuery(id+"F21.imprint","IMPRINT",FACE,{"disambiguationData":[TD([[makeQuery(id+"F21.imprint","IMPRINT",EDGE,{"derivedFrom":subQ7}),1.0]])]});}
            var Q1;
            {var subQ0=sQuery(id+"F21.wireOp",EDGE,"E120.top");Q1=makeQuery(id+"F21.imprint","IMPRINT",FACE,{"disambiguationData":[TD([[makeQuery(id+"F21.imprint","IMPRINT",EDGE,{"derivedFrom":subQ0}),-1.0]])]});}
            var Q2;
            Q2=makeQuery(id+"F21.imprint","IMPRINT",FACE,{"disambiguationData":[TD([[makeQuery(id+"F21.imprint","IMPRINT",EDGE,{"derivedFrom":sQuery(id+"F21.wireOp",EDGE,"E112")}),-1.0]])]});
            var Q3;
            {var subQ1=sQuery(id+"F21.wireOp",EDGE,"E117");Q3=makeQuery(id+"F21.imprint","IMPRINT",FACE,{"disambiguationData":[TD([[makeQuery(id+"F21.imprint","IMPRINT",EDGE,{"derivedFrom":subQ1}),-1.0]])]});}
            var Q4;
            {var subQ3=sQuery(id+"F21.wireOp",EDGE,"E118");Q4=makeQuery(id+"F21.imprint","IMPRINT",FACE,{"disambiguationData":[TD([[makeQuery(id+"F21.imprint","IMPRINT",EDGE,{"derivedFrom":subQ3}),-1.0]])]});}
            var Q5;
            {var subQ0=sQuery(id+"F21.wireOp",EDGE,"E145.top");Q5=makeQuery(id+"F21.imprint","IMPRINT",FACE,{"disambiguationData":[TD([[makeQuery(id+"F21.imprint","IMPRINT",EDGE,{"derivedFrom":subQ0}),-1.0]])]});}
            var Q6;
            {var subQ10=sQuery(id+"F21.wireOp",EDGE,"E162.MirrorCS");Q6=makeQuery(id+"F21.imprint","IMPRINT",FACE,{"disambiguationData":[TD([[makeQuery(id+"F21.imprint","IMPRINT",EDGE,{"derivedFrom":subQ10}),1.0]])]});}
            var Q7;
            {var subQ4=sQuery(id+"F21.wireOp",EDGE,"E140.left");Q7=makeQuery(id+"F21.imprint","IMPRINT",FACE,{"disambiguationData":[TD([[makeQuery(id+"F21.imprint","IMPRINT",EDGE,{"derivedFrom":subQ4}),-1.0]])]});}
            var Q8;
            {var subQ5=sQuery(id+"F21.wireOp",EDGE,"E140.right");Q8=makeQuery(id+"F21.imprint","IMPRINT",FACE,{"disambiguationData":[TD([[makeQuery(id+"F21.imprint","IMPRINT",EDGE,{"derivedFrom":subQ5}),1.0]])]});}
            var Q9;
            Q9=makeQuery(id+"F21.imprint","IMPRINT",FACE,{"disambiguationData":[TD([[makeQuery(id+"F21.imprint","IMPRINT",EDGE,{"derivedFrom":sQuery(id+"F21.wireOp",EDGE,"E137")}),-1.0]])]});
            extrude(context, id + "F22", {"entities" : qUnion([Q0, Q1, Q2, Q3, Q4, Q5, Q6, Q7, Q8, Q9]), "depth" : 266.7 * mm, "offsetDistance" : 25.4 * mm});
        }
        {
            var Q0;
            Q0=qCreatedBy(makeId("Front.planeOp"),FACE);
            var sketch = newSketch(context, id + "F23", { "sketchPlane" : qUnion([Q0])});
            skLineSegment(sketch, "E165.bottom", {"start": v(-142.55, 21.08) * mm, "end": v(-127.3, 21.08) * mm});
            skLineSegment(sketch, "E165.top", {"start": v(-142.55, 17.9) * mm, "end": v(-127.3, 17.9) * mm});
            skLineSegment(sketch, "E165.left", {"start": v(-142.55, 21.08) * mm, "end": v(-142.55, 17.9) * mm});
            skLineSegment(sketch, "E165.right", {"start": v(-127.3, 21.08) * mm, "end": v(-127.3, 17.9) * mm});
            skSolve(sketch);
        }
        {
            var Q0;
            Q0=makeQuery(id+"F23.imprint","IMPRINT",FACE,{"disambiguationData":[TD([[makeQuery(id+"F23.imprint","IMPRINT",EDGE,{"derivedFrom":sQuery(id+"F23.wireOp",EDGE,"E165.bottom")}),-1.0]])]});
            extrude(context, id + "F24", {"entities" : qUnion([Q0]), "depth" : 812.8 * mm, "offsetDistance" : 25.4 * mm});
        }
        {
            var Q0;
            Q0=qCreatedBy(makeId("Front.planeOp"),FACE);
            var sketch = newSketch(context, id + "F25", { "sketchPlane" : qUnion([Q0])});
            skLineSegment(sketch, "E166.bottom", {"start": v(-185.33, 19.8) * mm, "end": v(-170.09, 19.8) * mm});
            skLineSegment(sketch, "E166.top", {"start": v(-185.33, 16.63) * mm, "end": v(-170.09, 16.63) * mm});
            skLineSegment(sketch, "E166.left", {"start": v(-185.33, 19.8) * mm, "end": v(-185.33, 16.63) * mm});
            skLineSegment(sketch, "E166.right", {"start": v(-170.09, 19.8) * mm, "end": v(-170.09, 16.63) * mm});
            skSolve(sketch);
        }
        {
            var Q0;
            Q0=makeQuery(id+"F25.imprint","IMPRINT",FACE,{"disambiguationData":[TD([[makeQuery(id+"F25.imprint","IMPRINT",EDGE,{"derivedFrom":sQuery(id+"F25.wireOp",EDGE,"E166.bottom")}),-1.0]])]});
            extrude(context, id + "F26", {"entities" : qUnion([Q0]), "depth" : 812.8 * mm, "offsetDistance" : 25.4 * mm});
        }
        {
            var Q0;
            Q0=makeQuery(id+"F12.opExtrude","CAP_FACE",FACE,{"disambiguationData":[OSD([sQuery(id+"F11.wireOp",EDGE,"E96.bottom"),sQuery(id+"F11.wireOp",EDGE,"E96.top"),sQuery(id+"F11.wireOp",EDGE,"E96.left"),sQuery(id+"F11.wireOp",EDGE,"E96.right"),sQuery(id+"F11.wireOp",EDGE,"E102.0"),sQuery(id+"F11.wireOp",EDGE,"E102.1"),sQuery(id+"F11.wireOp",EDGE,"E102.2")])],"isStart":false});
            var sketch = newSketch(context, id + "F27", { "sketchPlane" : qUnion([Q0])});
            skLineSegment(sketch, "E167.bottom", {"start": v(482.81, 647.19) * mm, "end": v(559.01, 647.19) * mm});
            skLineSegment(sketch, "E167.top", {"start": v(482.81, 596.39) * mm, "end": v(559.01, 596.39) * mm});
            skLineSegment(sketch, "E167.left", {"start": v(482.81, 647.19) * mm, "end": v(482.81, 596.39) * mm});
            skLineSegment(sketch, "E167.right", {"start": v(559.01, 647.19) * mm, "end": v(559.01, 596.39) * mm});
            skLineSegment(sketch, "E168", {"start": v(482.81, 647.19) * mm, "end": v(559.01, 596.39) * mm});
            skLineSegment(sketch, "E169", {"start": v(559.01, 647.19) * mm, "end": v(482.81, 596.39) * mm});
            skCircle(sketch, "E170", {"center": v(520.91, 621.79) * mm, "radius": 6.35 * mm});
            skSolve(sketch);
        }
        {
            var Q0;
            {var subQ0=sQuery(id+"F27.wireOp",EDGE,"E170");var subQ1=sQuery(id+"F27.wireOp",EDGE,"E168");var subQ2=makeQuery(id+"F27.imprint","INTERSECT",VERTEX,{"disambiguationData":[OD(0.0)],"derivedFrom":[subQ1,subQ0]});Q0=makeQuery(id+"F27.imprint","IMPRINT",FACE,{"disambiguationData":[TD([[makeQuery(id+"F27.imprint","IMPRINT",EDGE,{"disambiguationData":[TD([[subQ2,1.0]])],"derivedFrom":subQ1}),1.0]])]});}
            var Q1;
            {var subQ0=sQuery(id+"F27.wireOp",EDGE,"E170");var subQ1=sQuery(id+"F27.wireOp",EDGE,"E168");var subQ2=makeQuery(id+"F27.imprint","INTERSECT",VERTEX,{"disambiguationData":[OD(0.0)],"derivedFrom":[subQ1,subQ0]});Q1=makeQuery(id+"F27.imprint","IMPRINT",FACE,{"disambiguationData":[TD([[makeQuery(id+"F27.imprint","IMPRINT",EDGE,{"disambiguationData":[TD([[subQ2,1.0]])],"derivedFrom":subQ1}),-1.0]])]});}
            var Q2;
            {var subQ3=makeQuery(id+"F12.opExtrude","CAP_EDGE",EDGE,{"disambiguationData":[OSD([sQuery(id+"F11.wireOp",EDGE,"E102.0")])],"isStart":false});var subQ9=sQuery(id+"F27.wireOp",EDGE,"E167.top");var subQ10=makeQuery(id+"F27.imprint","INTERSECT",VERTEX,{"derivedFrom":[subQ3,subQ9]});Q2=makeQuery(id+"F27.imprint","IMPRINT",FACE,{"disambiguationData":[TD([[makeQuery(id+"F27.imprint","IMPRINT",EDGE,{"disambiguationData":[TD([[subQ10,-1.0]])],"derivedFrom":subQ9}),1.0]])]});}
            var Q3;
            {var subQ0=sQuery(id+"F27.wireOp",EDGE,"E170");var subQ1=sQuery(id+"F27.wireOp",EDGE,"E168");var subQ2=makeQuery(id+"F27.imprint","INTERSECT",VERTEX,{"disambiguationData":[OD(1.0)],"derivedFrom":[subQ1,subQ0]});Q3=makeQuery(id+"F27.imprint","IMPRINT",FACE,{"disambiguationData":[TD([[makeQuery(id+"F27.imprint","IMPRINT",EDGE,{"disambiguationData":[TD([[subQ2,-1.0]])],"derivedFrom":subQ1}),1.0]])]});}
            extrude(context, id + "F28", {"entities" : qUnion([Q0, Q1, Q2, Q3]), "operationType" : NewBodyOperationType.ADD, "oppositeDirection" : true, "depth" : 12.7 * mm, "offsetDistance" : 25.4 * mm});
        }
        {
            var Q0;
            Q0=makeQuery(id+"F12.opExtrude","CAP_FACE",FACE,{"disambiguationData":[OSD([sQuery(id+"F11.wireOp",EDGE,"E97.bottom"),sQuery(id+"F11.wireOp",EDGE,"E97.top"),sQuery(id+"F11.wireOp",EDGE,"E97.left"),sQuery(id+"F11.wireOp",EDGE,"E97.right"),sQuery(id+"F11.wireOp",EDGE,"E101.0"),sQuery(id+"F11.wireOp",EDGE,"E101.1"),sQuery(id+"F11.wireOp",EDGE,"E101.2")])],"isStart":false});
            var sketch = newSketch(context, id + "F29", { "sketchPlane" : qUnion([Q0])});
            skLineSegment(sketch, "E171.bottom", {"start": v(482.81, 88.39) * mm, "end": v(559.01, 88.39) * mm});
            skLineSegment(sketch, "E171.top", {"start": v(482.81, 37.59) * mm, "end": v(559.01, 37.59) * mm});
            skLineSegment(sketch, "E171.left", {"start": v(482.81, 88.39) * mm, "end": v(482.81, 37.59) * mm});
            skLineSegment(sketch, "E171.right", {"start": v(559.01, 88.39) * mm, "end": v(559.01, 37.59) * mm});
            skLineSegment(sketch, "E172", {"start": v(482.81, 88.39) * mm, "end": v(559.01, 37.59) * mm});
            skLineSegment(sketch, "E173", {"start": v(559.01, 88.39) * mm, "end": v(482.81, 37.59) * mm});
            skCircle(sketch, "E174", {"center": v(520.91, 62.99) * mm, "radius": 6.35 * mm});
            skSolve(sketch);
        }
        {
            var Q0;
            {var subQ5=makeQuery(id+"F12.opExtrude","CAP_EDGE",EDGE,{"disambiguationData":[OSD([sQuery(id+"F11.wireOp",EDGE,"E101.0")])],"isStart":false});var subQ9=sQuery(id+"F29.wireOp",EDGE,"E171.bottom");var subQ10=makeQuery(id+"F29.imprint","INTERSECT",VERTEX,{"derivedFrom":[subQ5,subQ9]});Q0=makeQuery(id+"F29.imprint","IMPRINT",FACE,{"disambiguationData":[TD([[makeQuery(id+"F29.imprint","IMPRINT",EDGE,{"disambiguationData":[TD([[subQ10,-1.0]])],"derivedFrom":subQ9}),-1.0]])]});}
            var Q1;
            {var subQ0=sQuery(id+"F29.wireOp",EDGE,"E174");var subQ1=sQuery(id+"F29.wireOp",EDGE,"E172");var subQ2=makeQuery(id+"F29.imprint","INTERSECT",VERTEX,{"disambiguationData":[OD(0.0)],"derivedFrom":[subQ1,subQ0]});Q1=makeQuery(id+"F29.imprint","IMPRINT",FACE,{"disambiguationData":[TD([[makeQuery(id+"F29.imprint","IMPRINT",EDGE,{"disambiguationData":[TD([[subQ2,1.0]])],"derivedFrom":subQ1}),-1.0]])]});}
            var Q2;
            {var subQ0=sQuery(id+"F29.wireOp",EDGE,"E174");var subQ1=sQuery(id+"F29.wireOp",EDGE,"E172");var subQ2=makeQuery(id+"F29.imprint","INTERSECT",VERTEX,{"disambiguationData":[OD(1.0)],"derivedFrom":[subQ1,subQ0]});Q2=makeQuery(id+"F29.imprint","IMPRINT",FACE,{"disambiguationData":[TD([[makeQuery(id+"F29.imprint","IMPRINT",EDGE,{"disambiguationData":[TD([[subQ2,-1.0]])],"derivedFrom":subQ1}),-1.0]])]});}
            var Q3;
            {var subQ0=sQuery(id+"F29.wireOp",EDGE,"E174");var subQ1=sQuery(id+"F29.wireOp",EDGE,"E172");var subQ2=makeQuery(id+"F29.imprint","INTERSECT",VERTEX,{"disambiguationData":[OD(1.0)],"derivedFrom":[subQ1,subQ0]});Q3=makeQuery(id+"F29.imprint","IMPRINT",FACE,{"disambiguationData":[TD([[makeQuery(id+"F29.imprint","IMPRINT",EDGE,{"disambiguationData":[TD([[subQ2,-1.0]])],"derivedFrom":subQ1}),1.0]])]});}
            extrude(context, id + "F30", {"entities" : qUnion([Q0, Q1, Q2, Q3]), "operationType" : NewBodyOperationType.ADD, "oppositeDirection" : true, "depth" : 12.7 * mm, "offsetDistance" : 25.4 * mm});
        }
        {
            var Q0;
            Q0=makeQuery(id+"F12.opExtrude","CAP_FACE",FACE,{"disambiguationData":[OSD([sQuery(id+"F11.wireOp",EDGE,"E99.bottom"),sQuery(id+"F11.wireOp",EDGE,"E99.top"),sQuery(id+"F11.wireOp",EDGE,"E99.left"),sQuery(id+"F11.wireOp",EDGE,"E99.right"),sQuery(id+"F11.wireOp",EDGE,"E103.0"),sQuery(id+"F11.wireOp",EDGE,"E103.1"),sQuery(id+"F11.wireOp",EDGE,"E103.2")])],"isStart":false});
            var sketch = newSketch(context, id + "F31", { "sketchPlane" : qUnion([Q0])});
            skLineSegment(sketch, "E175.bottom", {"start": v(1321.01, 647.19) * mm, "end": v(1397.21, 647.19) * mm});
            skLineSegment(sketch, "E175.top", {"start": v(1321.01, 596.39) * mm, "end": v(1397.21, 596.39) * mm});
            skLineSegment(sketch, "E175.left", {"start": v(1321.01, 647.19) * mm, "end": v(1321.01, 596.39) * mm});
            skLineSegment(sketch, "E175.right", {"start": v(1397.21, 647.19) * mm, "end": v(1397.21, 596.39) * mm});
            skLineSegment(sketch, "E176", {"start": v(1321.01, 647.19) * mm, "end": v(1397.21, 596.39) * mm});
            skLineSegment(sketch, "E177", {"start": v(1397.21, 647.19) * mm, "end": v(1321.01, 596.39) * mm});
            skCircle(sketch, "E178", {"center": v(1359.11, 621.79) * mm, "radius": 6.35 * mm});
            skSolve(sketch);
        }
        {
            var Q0;
            {var subQ0=sQuery(id+"F31.wireOp",EDGE,"E178");var subQ1=sQuery(id+"F31.wireOp",EDGE,"E176");var subQ2=makeQuery(id+"F31.imprint","INTERSECT",VERTEX,{"disambiguationData":[OD(0.0)],"derivedFrom":[subQ1,subQ0]});Q0=makeQuery(id+"F31.imprint","IMPRINT",FACE,{"disambiguationData":[TD([[makeQuery(id+"F31.imprint","IMPRINT",EDGE,{"disambiguationData":[TD([[subQ2,1.0]])],"derivedFrom":subQ1}),-1.0]])]});}
            var Q1;
            {var subQ0=sQuery(id+"F31.wireOp",EDGE,"E178");var subQ1=sQuery(id+"F31.wireOp",EDGE,"E176");var subQ2=makeQuery(id+"F31.imprint","INTERSECT",VERTEX,{"disambiguationData":[OD(0.0)],"derivedFrom":[subQ1,subQ0]});Q1=makeQuery(id+"F31.imprint","IMPRINT",FACE,{"disambiguationData":[TD([[makeQuery(id+"F31.imprint","IMPRINT",EDGE,{"disambiguationData":[TD([[subQ2,1.0]])],"derivedFrom":subQ1}),1.0]])]});}
            var Q2;
            {var subQ0=sQuery(id+"F31.wireOp",EDGE,"E178");var subQ1=sQuery(id+"F31.wireOp",EDGE,"E176");var subQ2=makeQuery(id+"F31.imprint","INTERSECT",VERTEX,{"disambiguationData":[OD(1.0)],"derivedFrom":[subQ1,subQ0]});Q2=makeQuery(id+"F31.imprint","IMPRINT",FACE,{"disambiguationData":[TD([[makeQuery(id+"F31.imprint","IMPRINT",EDGE,{"disambiguationData":[TD([[subQ2,-1.0]])],"derivedFrom":subQ1}),1.0]])]});}
            var Q3;
            {var subQ5=makeQuery(id+"F12.opExtrude","CAP_EDGE",EDGE,{"disambiguationData":[OSD([sQuery(id+"F11.wireOp",EDGE,"E103.2")])],"isStart":false});var subQ7=makeQuery(id+"F12.opExtrude","CAP_EDGE",EDGE,{"disambiguationData":[OSD([sQuery(id+"F11.wireOp",EDGE,"E103.0")])],"isStart":false});var subQ9=sQuery(id+"F31.wireOp",EDGE,"E175.top");var subQ10=makeQuery(id+"F31.imprint","INTERSECT",VERTEX,{"derivedFrom":[subQ7,subQ9]});var subQ11=makeQuery(id+"F31.imprint","INTERSECT",VERTEX,{"derivedFrom":[subQ5,subQ9]});Q3=makeQuery(id+"F31.imprint","IMPRINT",FACE,{"disambiguationData":[TD([[makeQuery(id+"F31.imprint","IMPRINT",EDGE,{"disambiguationData":[TD([[subQ10,-1.0],[subQ11,1.0]])],"derivedFrom":subQ9}),1.0]])]});}
            extrude(context, id + "F32", {"entities" : qUnion([Q0, Q1, Q2, Q3]), "operationType" : NewBodyOperationType.ADD, "oppositeDirection" : true, "depth" : 12.7 * mm, "offsetDistance" : 25.4 * mm});
        }
        {
            var Q0;
            Q0=makeQuery(id+"F12.opExtrude","CAP_FACE",FACE,{"disambiguationData":[OSD([sQuery(id+"F11.wireOp",EDGE,"E98.bottom"),sQuery(id+"F11.wireOp",EDGE,"E98.top"),sQuery(id+"F11.wireOp",EDGE,"E98.left"),sQuery(id+"F11.wireOp",EDGE,"E98.right"),sQuery(id+"F11.wireOp",EDGE,"E100.0"),sQuery(id+"F11.wireOp",EDGE,"E100.1"),sQuery(id+"F11.wireOp",EDGE,"E100.2")])],"isStart":false});
            var sketch = newSketch(context, id + "F33", { "sketchPlane" : qUnion([Q0])});
            skLineSegment(sketch, "E179.bottom", {"start": v(1321.01, 88.39) * mm, "end": v(1397.21, 88.39) * mm});
            skLineSegment(sketch, "E179.top", {"start": v(1321.01, 37.59) * mm, "end": v(1397.21, 37.59) * mm});
            skLineSegment(sketch, "E179.left", {"start": v(1321.01, 88.39) * mm, "end": v(1321.01, 37.59) * mm});
            skLineSegment(sketch, "E179.right", {"start": v(1397.21, 88.39) * mm, "end": v(1397.21, 37.59) * mm});
            skLineSegment(sketch, "E180", {"start": v(1321.01, 88.39) * mm, "end": v(1397.21, 37.59) * mm});
            skLineSegment(sketch, "E181", {"start": v(1397.21, 88.39) * mm, "end": v(1321.01, 37.59) * mm});
            skCircle(sketch, "E182", {"center": v(1359.11, 62.99) * mm, "radius": 6.35 * mm});
            skSolve(sketch);
        }
        {
            var Q0;
            {var subQ5=makeQuery(id+"F12.opExtrude","CAP_EDGE",EDGE,{"disambiguationData":[OSD([sQuery(id+"F11.wireOp",EDGE,"E100.0")])],"isStart":false});var subQ7=makeQuery(id+"F12.opExtrude","CAP_EDGE",EDGE,{"disambiguationData":[OSD([sQuery(id+"F11.wireOp",EDGE,"E100.2")])],"isStart":false});var subQ9=sQuery(id+"F33.wireOp",EDGE,"E179.bottom");var subQ10=makeQuery(id+"F33.imprint","INTERSECT",VERTEX,{"derivedFrom":[subQ5,subQ9]});var subQ11=makeQuery(id+"F33.imprint","INTERSECT",VERTEX,{"derivedFrom":[subQ7,subQ9]});Q0=makeQuery(id+"F33.imprint","IMPRINT",FACE,{"disambiguationData":[TD([[makeQuery(id+"F33.imprint","IMPRINT",EDGE,{"disambiguationData":[TD([[subQ10,-1.0],[subQ11,1.0]])],"derivedFrom":subQ9}),-1.0]])]});}
            var Q1;
            {var subQ0=sQuery(id+"F33.wireOp",EDGE,"E182");var subQ1=sQuery(id+"F33.wireOp",EDGE,"E180");var subQ2=makeQuery(id+"F33.imprint","INTERSECT",VERTEX,{"disambiguationData":[OD(0.0)],"derivedFrom":[subQ1,subQ0]});Q1=makeQuery(id+"F33.imprint","IMPRINT",FACE,{"disambiguationData":[TD([[makeQuery(id+"F33.imprint","IMPRINT",EDGE,{"disambiguationData":[TD([[subQ2,1.0]])],"derivedFrom":subQ1}),-1.0]])]});}
            var Q2;
            {var subQ0=sQuery(id+"F33.wireOp",EDGE,"E182");var subQ1=sQuery(id+"F33.wireOp",EDGE,"E180");var subQ2=makeQuery(id+"F33.imprint","INTERSECT",VERTEX,{"disambiguationData":[OD(1.0)],"derivedFrom":[subQ1,subQ0]});Q2=makeQuery(id+"F33.imprint","IMPRINT",FACE,{"disambiguationData":[TD([[makeQuery(id+"F33.imprint","IMPRINT",EDGE,{"disambiguationData":[TD([[subQ2,-1.0]])],"derivedFrom":subQ1}),-1.0]])]});}
            var Q3;
            {var subQ0=sQuery(id+"F33.wireOp",EDGE,"E182");var subQ1=sQuery(id+"F33.wireOp",EDGE,"E180");var subQ2=makeQuery(id+"F33.imprint","INTERSECT",VERTEX,{"disambiguationData":[OD(1.0)],"derivedFrom":[subQ1,subQ0]});Q3=makeQuery(id+"F33.imprint","IMPRINT",FACE,{"disambiguationData":[TD([[makeQuery(id+"F33.imprint","IMPRINT",EDGE,{"disambiguationData":[TD([[subQ2,-1.0]])],"derivedFrom":subQ1}),1.0]])]});}
            extrude(context, id + "F34", {"entities" : qUnion([Q0, Q1, Q2, Q3]), "operationType" : NewBodyOperationType.ADD, "oppositeDirection" : true, "depth" : 12.7 * mm, "offsetDistance" : 25.4 * mm});
        }
        {
            var Q0;
            Q0=qCreatedBy(makeId("Top.planeOp"),FACE);
            var sketch = newSketch(context, id + "F35", { "sketchPlane" : qUnion([Q0])});
            skLineSegment(sketch, "E183.bottom", {"start": v(-346.19, -10.4) * mm, "end": v(-295.39, -10.4) * mm});
            skLineSegment(sketch, "E183.top", {"start": v(-346.19, -607.3) * mm, "end": v(-295.39, -607.3) * mm});
            skLineSegment(sketch, "E183.left", {"start": v(-346.19, -10.4) * mm, "end": v(-346.19, -607.3) * mm});
            skLineSegment(sketch, "E183.right", {"start": v(-295.39, -10.4) * mm, "end": v(-295.39, -607.3) * mm});
            skSolve(sketch);
        }
        {
            var Q0;
            Q0=makeQuery(id+"F35.imprint","IMPRINT",FACE,{"disambiguationData":[TD([[makeQuery(id+"F35.imprint","IMPRINT",EDGE,{"derivedFrom":sQuery(id+"F35.wireOp",EDGE,"E183.bottom")}),-1.0]])]});
            extrude(context, id + "F36", {"entities" : qUnion([Q0]), "depth" : 50.8 * mm, "offsetDistance" : 25.4 * mm});
        }
    });
